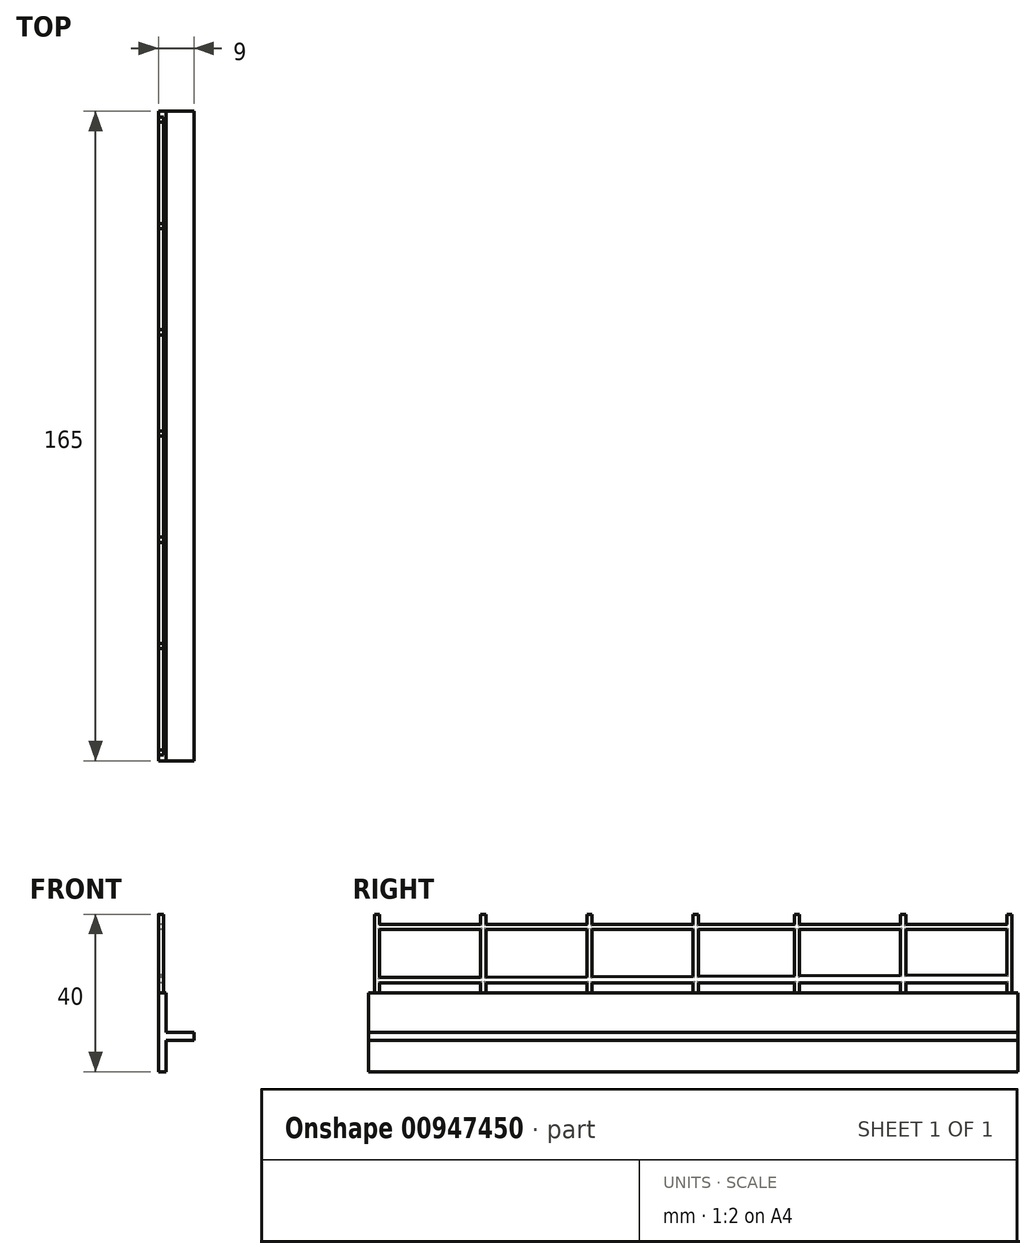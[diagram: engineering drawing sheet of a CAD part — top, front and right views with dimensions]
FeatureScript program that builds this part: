
annotation { "Feature Type Name" : "Feature", "Feature Type Description" : "" }
export const myFeature = defineFeature(function(context is Context, id is Id, definition is map)
    precondition{}
    {
        {
            var Q0;
            Q0=qCreatedBy(makeId("Front.planeOp"),FACE);
            var sketch = newSketch(context, id + "F0", { "sketchPlane" : qUnion([Q0])});
            skLineSegment(sketch, "E0", {"start": v(0, 0) * mm, "end": v(0, 10) * mm});
            skLineSegment(sketch, "E1", {"start": v(0, 0) * mm, "end": v(7, 0) * mm});
            skLineSegment(sketch, "E2", {"start": v(7, 0) * mm, "end": v(7, -2) * mm});
            skLineSegment(sketch, "E3", {"start": v(7, -2) * mm, "end": v(0, -2) * mm});
            skLineSegment(sketch, "E4", {"start": v(0, 10) * mm, "end": v(-2, 10) * mm});
            skLineSegment(sketch, "E5", {"start": v(0, -2) * mm, "end": v(0, -10) * mm});
            skLineSegment(sketch, "E6", {"start": v(-2, 10) * mm, "end": v(-2, -10) * mm});
            skLineSegment(sketch, "E7", {"start": v(0, -10) * mm, "end": v(-2, -10) * mm});
            skSolve(sketch);
        }
        {
            var Q0;
            Q0=makeQuery(id+"F0.imprint","IMPRINT",FACE,{"disambiguationData":[TD([[makeQuery(id+"F0.imprint","IMPRINT",EDGE,{"derivedFrom":sQuery(id+"F0.wireOp",EDGE,"E0")}),1.0]])]});
            extrude(context, id + "F1", {"entities" : qUnion([Q0]), "depth" : 165 * mm, "offsetDistance" : 25 * mm});
        }
        {
            var Q0;
            Q0=makeQuery(id+"F1.opExtrude","SWEPT_FACE",FACE,{"disambiguationData":[OSD([sQuery(id+"F0.wireOp",EDGE,"E4")])]});
            var sketch = newSketch(context, id + "F2", { "sketchPlane" : qUnion([Q0])});
            skLineSegment(sketch, "E8", {"start": v(0, 0) * mm, "end": v(0, -82.5) * mm});
            skLineSegment(sketch, "E9", {"start": v(0, -82.5) * mm, "end": v(0, -55.5) * mm});
            skLineSegment(sketch, "E10", {"start": v(0, -55.5) * mm, "end": v(0, -28.5) * mm});
            skLineSegment(sketch, "E11", {"start": v(0, -28.5) * mm, "end": v(0, -1.5) * mm});
            skLineSegment(sketch, "E12", {"start": v(0, -82.5) * mm, "end": v(0, -109.5) * mm});
            skLineSegment(sketch, "E13", {"start": v(0, -109.5) * mm, "end": v(0, -136.5) * mm});
            skLineSegment(sketch, "E14", {"start": v(0, -136.5) * mm, "end": v(0, -163.5) * mm});
            skLineSegment(sketch, "E15", {"start": v(-2, 0) * mm, "end": v(-0.7, 0) * mm});
            skLineSegment(sketch, "E16", {"start": v(-0.7, 0) * mm, "end": v(-0.7, -165) * mm});
            skLineSegment(sketch, "E17.bottom", {"start": v(-0.7, -1.5) * mm, "end": v(-2, -1.5) * mm});
            skLineSegment(sketch, "E17.top", {"start": v(-0.7, -2.8) * mm, "end": v(-2, -2.8) * mm});
            skLineSegment(sketch, "E17.left", {"start": v(-0.7, -1.5) * mm, "end": v(-0.7, -2.8) * mm});
            skLineSegment(sketch, "E17.right", {"start": v(-2, -1.5) * mm, "end": v(-2, -2.8) * mm});
            skLineSegment(sketch, "E18.bottom", {"start": v(-0.7, -28.5) * mm, "end": v(-2, -28.5) * mm});
            skLineSegment(sketch, "E18.top", {"start": v(-0.7, -29.8) * mm, "end": v(-2, -29.8) * mm});
            skLineSegment(sketch, "E18.left", {"start": v(-0.7, -28.5) * mm, "end": v(-0.7, -29.8) * mm});
            skLineSegment(sketch, "E18.right", {"start": v(-2, -28.5) * mm, "end": v(-2, -29.8) * mm});
            skLineSegment(sketch, "E19.bottom", {"start": v(-0.7, -55.5) * mm, "end": v(-2, -55.5) * mm});
            skLineSegment(sketch, "E19.top", {"start": v(-0.7, -56.8) * mm, "end": v(-2, -56.8) * mm});
            skLineSegment(sketch, "E19.left", {"start": v(-0.7, -55.5) * mm, "end": v(-0.7, -56.8) * mm});
            skLineSegment(sketch, "E19.right", {"start": v(-2, -55.5) * mm, "end": v(-2, -56.8) * mm});
            skLineSegment(sketch, "E20.bottom", {"start": v(-0.7, -82.5) * mm, "end": v(-2, -82.5) * mm});
            skLineSegment(sketch, "E20.top", {"start": v(-0.7, -81.2) * mm, "end": v(-2, -81.2) * mm});
            skLineSegment(sketch, "E20.left", {"start": v(-0.7, -82.5) * mm, "end": v(-0.7, -81.2) * mm});
            skLineSegment(sketch, "E20.right", {"start": v(-2, -82.5) * mm, "end": v(-2, -81.2) * mm});
            skLineSegment(sketch, "E21.bottom", {"start": v(-0.7, -109.5) * mm, "end": v(-2, -109.5) * mm});
            skLineSegment(sketch, "E21.top", {"start": v(-0.7, -108.2) * mm, "end": v(-2, -108.2) * mm});
            skLineSegment(sketch, "E21.left", {"start": v(-0.7, -109.5) * mm, "end": v(-0.7, -108.2) * mm});
            skLineSegment(sketch, "E21.right", {"start": v(-2, -109.5) * mm, "end": v(-2, -108.2) * mm});
            skLineSegment(sketch, "E22.bottom", {"start": v(-0.7, -136.5) * mm, "end": v(-2, -136.5) * mm});
            skLineSegment(sketch, "E22.top", {"start": v(-0.7, -135.2) * mm, "end": v(-2, -135.2) * mm});
            skLineSegment(sketch, "E22.left", {"start": v(-0.7, -136.5) * mm, "end": v(-0.7, -135.2) * mm});
            skLineSegment(sketch, "E22.right", {"start": v(-2, -136.5) * mm, "end": v(-2, -135.2) * mm});
            skLineSegment(sketch, "E23.bottom", {"start": v(-0.7, -163.5) * mm, "end": v(-2, -163.5) * mm});
            skLineSegment(sketch, "E23.top", {"start": v(-0.7, -162.2) * mm, "end": v(-2, -162.2) * mm});
            skLineSegment(sketch, "E23.left", {"start": v(-0.7, -163.5) * mm, "end": v(-0.7, -162.2) * mm});
            skLineSegment(sketch, "E23.right", {"start": v(-2, -163.5) * mm, "end": v(-2, -162.2) * mm});
            skSolve(sketch);
        }
        {
            var Q0;
            Q0=makeQuery(id+"F2.imprint","IMPRINT",FACE,{"disambiguationData":[TD([[makeQuery(id+"F2.imprint","IMPRINT",EDGE,{"derivedFrom":sQuery(id+"F2.wireOp",EDGE,"E17.bottom")}),1.0]])]});
            var Q1;
            Q1=makeQuery(id+"F2.imprint","IMPRINT",FACE,{"disambiguationData":[TD([[makeQuery(id+"F2.imprint","IMPRINT",EDGE,{"derivedFrom":sQuery(id+"F2.wireOp",EDGE,"E18.bottom")}),1.0]])]});
            var Q2;
            Q2=makeQuery(id+"F2.imprint","IMPRINT",FACE,{"disambiguationData":[TD([[makeQuery(id+"F2.imprint","IMPRINT",EDGE,{"derivedFrom":sQuery(id+"F2.wireOp",EDGE,"E19.bottom")}),1.0]])]});
            var Q3;
            Q3=makeQuery(id+"F2.imprint","IMPRINT",FACE,{"disambiguationData":[TD([[makeQuery(id+"F2.imprint","IMPRINT",EDGE,{"derivedFrom":sQuery(id+"F2.wireOp",EDGE,"E20.bottom")}),-1.0]])]});
            var Q4;
            Q4=makeQuery(id+"F2.imprint","IMPRINT",FACE,{"disambiguationData":[TD([[makeQuery(id+"F2.imprint","IMPRINT",EDGE,{"derivedFrom":sQuery(id+"F2.wireOp",EDGE,"E21.bottom")}),-1.0]])]});
            var Q5;
            Q5=makeQuery(id+"F2.imprint","IMPRINT",FACE,{"disambiguationData":[TD([[makeQuery(id+"F2.imprint","IMPRINT",EDGE,{"derivedFrom":sQuery(id+"F2.wireOp",EDGE,"E22.bottom")}),-1.0]])]});
            var Q6;
            Q6=makeQuery(id+"F2.imprint","IMPRINT",FACE,{"disambiguationData":[TD([[makeQuery(id+"F2.imprint","IMPRINT",EDGE,{"derivedFrom":sQuery(id+"F2.wireOp",EDGE,"E23.bottom")}),-1.0]])]});
            extrude(context, id + "F3", {"entities" : qUnion([Q0, Q1, Q2, Q3, Q4, Q5, Q6]), "operationType" : NewBodyOperationType.ADD, "depth" : 20 * mm, "offsetDistance" : 25 * mm});
        }
        {
            var Q0;
            Q0=makeQuery(id+"F3.boolean.opBoolean","MERGE",FACE,{"derivedFrom":[makeQuery(id+"F1.opExtrude","SWEPT_FACE",FACE,{"disambiguationData":[OSD([sQuery(id+"F0.wireOp",EDGE,"E6")])]}),makeQuery(id+"F3.opExtrude","SWEPT_FACE",FACE,{"disambiguationData":[OSD([sQuery(id+"F2.wireOp",EDGE,"E17.right")])]}),makeQuery(id+"F3.opExtrude","SWEPT_FACE",FACE,{"disambiguationData":[OSD([sQuery(id+"F2.wireOp",EDGE,"E18.right")])]}),makeQuery(id+"F3.opExtrude","SWEPT_FACE",FACE,{"disambiguationData":[OSD([sQuery(id+"F2.wireOp",EDGE,"E19.right")])]}),makeQuery(id+"F3.opExtrude","SWEPT_FACE",FACE,{"disambiguationData":[OSD([sQuery(id+"F2.wireOp",EDGE,"E20.right")])]}),makeQuery(id+"F3.opExtrude","SWEPT_FACE",FACE,{"disambiguationData":[OSD([sQuery(id+"F2.wireOp",EDGE,"E21.right")])]}),makeQuery(id+"F3.opExtrude","SWEPT_FACE",FACE,{"disambiguationData":[OSD([sQuery(id+"F2.wireOp",EDGE,"E22.right")])]}),makeQuery(id+"F3.opExtrude","SWEPT_FACE",FACE,{"disambiguationData":[OSD([sQuery(id+"F2.wireOp",EDGE,"E23.right")])]})]});
            var sketch = newSketch(context, id + "F4", { "sketchPlane" : qUnion([Q0])});
            skLineSegment(sketch, "E24", {"start": v(1.5, 10) * mm, "end": v(1.5, 12.6) * mm});
            skLineSegment(sketch, "E25", {"start": v(1.5, 12.6) * mm, "end": v(163.5, 12.6) * mm});
            skLineSegment(sketch, "E26", {"start": v(163.5, 12.6) * mm, "end": v(163.5, 13.9) * mm});
            skLineSegment(sketch, "E27", {"start": v(163.5, 13.9) * mm, "end": v(1.5, 14.56) * mm});
            skLineSegment(sketch, "E28", {"start": v(1.5, 30) * mm, "end": v(1.5, 27.4) * mm});
            skLineSegment(sketch, "E29", {"start": v(1.5, 27.4) * mm, "end": v(163.5, 27.4) * mm});
            skLineSegment(sketch, "E30", {"start": v(163.5, 27.4) * mm, "end": v(163.5, 26.1) * mm});
            skLineSegment(sketch, "E31", {"start": v(163.5, 26.1) * mm, "end": v(1.5, 26.1) * mm});
            skSolve(sketch);
        }
        {
            var Q0;
            {var subQ0=sQuery(id+"F4.wireOp",EDGE,"E25");var subQ1=sQuery(id+"F0.wireOp",EDGE,"E6");var subQ2=sQuery(id+"F0.wireOp",EDGE,"E4");var subQ3=makeQuery(id+"F3.opExtrude","SWEPT_EDGE",EDGE,{"disambiguationData":[OSD([subQ2,subQ1,sQuery(id+"F2.wireOp",EDGE,"E17.top"),sQuery(id+"F2.wireOp",EDGE,"E17.right")])]});var subQ4=makeQuery(id+"F4.imprint","INTERSECT",VERTEX,{"derivedFrom":[subQ3,subQ0]});Q0=makeQuery(id+"F4.imprint","IMPRINT",FACE,{"disambiguationData":[TD([[makeQuery(id+"F4.imprint","IMPRINT",EDGE,{"disambiguationData":[TD([[subQ4,-1.0]])],"derivedFrom":subQ0}),1.0]])]});}
            var Q1;
            {var subQ0=sQuery(id+"F4.wireOp",EDGE,"E29");var subQ1=sQuery(id+"F0.wireOp",EDGE,"E6");var subQ2=sQuery(id+"F0.wireOp",EDGE,"E4");var subQ3=makeQuery(id+"F3.opExtrude","SWEPT_EDGE",EDGE,{"disambiguationData":[OSD([subQ2,subQ1,sQuery(id+"F2.wireOp",EDGE,"E17.top"),sQuery(id+"F2.wireOp",EDGE,"E17.right")])]});var subQ4=makeQuery(id+"F4.imprint","INTERSECT",VERTEX,{"derivedFrom":[subQ3,subQ0]});Q1=makeQuery(id+"F4.imprint","IMPRINT",FACE,{"disambiguationData":[TD([[makeQuery(id+"F4.imprint","IMPRINT",EDGE,{"disambiguationData":[TD([[subQ4,-1.0]])],"derivedFrom":subQ0}),-1.0]])]});}
            var Q2;
            {var subQ0=sQuery(id+"F4.wireOp",EDGE,"E29");var subQ1=sQuery(id+"F0.wireOp",EDGE,"E6");var subQ2=sQuery(id+"F0.wireOp",EDGE,"E4");var subQ3=makeQuery(id+"F3.opExtrude","SWEPT_EDGE",EDGE,{"disambiguationData":[OSD([subQ2,subQ1,sQuery(id+"F2.wireOp",EDGE,"E18.top"),sQuery(id+"F2.wireOp",EDGE,"E18.right")])]});var subQ4=makeQuery(id+"F4.imprint","INTERSECT",VERTEX,{"derivedFrom":[subQ3,subQ0]});Q2=makeQuery(id+"F4.imprint","IMPRINT",FACE,{"disambiguationData":[TD([[makeQuery(id+"F4.imprint","IMPRINT",EDGE,{"disambiguationData":[TD([[subQ4,-1.0]])],"derivedFrom":subQ0}),-1.0]])]});}
            var Q3;
            {var subQ0=sQuery(id+"F4.wireOp",EDGE,"E25");var subQ1=sQuery(id+"F0.wireOp",EDGE,"E6");var subQ2=sQuery(id+"F0.wireOp",EDGE,"E4");var subQ3=makeQuery(id+"F3.opExtrude","SWEPT_EDGE",EDGE,{"disambiguationData":[OSD([subQ2,subQ1,sQuery(id+"F2.wireOp",EDGE,"E18.top"),sQuery(id+"F2.wireOp",EDGE,"E18.right")])]});var subQ4=makeQuery(id+"F4.imprint","INTERSECT",VERTEX,{"derivedFrom":[subQ3,subQ0]});Q3=makeQuery(id+"F4.imprint","IMPRINT",FACE,{"disambiguationData":[TD([[makeQuery(id+"F4.imprint","IMPRINT",EDGE,{"disambiguationData":[TD([[subQ4,-1.0]])],"derivedFrom":subQ0}),1.0]])]});}
            var Q4;
            {var subQ0=sQuery(id+"F4.wireOp",EDGE,"E29");var subQ1=sQuery(id+"F0.wireOp",EDGE,"E6");var subQ2=sQuery(id+"F0.wireOp",EDGE,"E4");var subQ3=makeQuery(id+"F3.opExtrude","SWEPT_EDGE",EDGE,{"disambiguationData":[OSD([subQ2,subQ1,sQuery(id+"F2.wireOp",EDGE,"E19.top"),sQuery(id+"F2.wireOp",EDGE,"E19.right")])]});var subQ4=makeQuery(id+"F4.imprint","INTERSECT",VERTEX,{"derivedFrom":[subQ3,subQ0]});Q4=makeQuery(id+"F4.imprint","IMPRINT",FACE,{"disambiguationData":[TD([[makeQuery(id+"F4.imprint","IMPRINT",EDGE,{"disambiguationData":[TD([[subQ4,-1.0]])],"derivedFrom":subQ0}),-1.0]])]});}
            var Q5;
            {var subQ0=sQuery(id+"F4.wireOp",EDGE,"E25");var subQ1=sQuery(id+"F0.wireOp",EDGE,"E6");var subQ2=sQuery(id+"F0.wireOp",EDGE,"E4");var subQ3=makeQuery(id+"F3.opExtrude","SWEPT_EDGE",EDGE,{"disambiguationData":[OSD([subQ2,subQ1,sQuery(id+"F2.wireOp",EDGE,"E19.top"),sQuery(id+"F2.wireOp",EDGE,"E19.right")])]});var subQ4=makeQuery(id+"F4.imprint","INTERSECT",VERTEX,{"derivedFrom":[subQ3,subQ0]});Q5=makeQuery(id+"F4.imprint","IMPRINT",FACE,{"disambiguationData":[TD([[makeQuery(id+"F4.imprint","IMPRINT",EDGE,{"disambiguationData":[TD([[subQ4,-1.0]])],"derivedFrom":subQ0}),1.0]])]});}
            var Q6;
            {var subQ0=sQuery(id+"F4.wireOp",EDGE,"E25");var subQ1=sQuery(id+"F0.wireOp",EDGE,"E6");var subQ2=sQuery(id+"F0.wireOp",EDGE,"E4");var subQ3=makeQuery(id+"F3.opExtrude","SWEPT_EDGE",EDGE,{"disambiguationData":[OSD([subQ2,subQ1,sQuery(id+"F2.wireOp",EDGE,"E20.bottom"),sQuery(id+"F2.wireOp",EDGE,"E20.right")])]});var subQ4=makeQuery(id+"F4.imprint","INTERSECT",VERTEX,{"derivedFrom":[subQ3,subQ0]});Q6=makeQuery(id+"F4.imprint","IMPRINT",FACE,{"disambiguationData":[TD([[makeQuery(id+"F4.imprint","IMPRINT",EDGE,{"disambiguationData":[TD([[subQ4,-1.0]])],"derivedFrom":subQ0}),1.0]])]});}
            var Q7;
            {var subQ0=sQuery(id+"F4.wireOp",EDGE,"E29");var subQ1=sQuery(id+"F0.wireOp",EDGE,"E6");var subQ2=sQuery(id+"F0.wireOp",EDGE,"E4");var subQ3=makeQuery(id+"F3.opExtrude","SWEPT_EDGE",EDGE,{"disambiguationData":[OSD([subQ2,subQ1,sQuery(id+"F2.wireOp",EDGE,"E20.bottom"),sQuery(id+"F2.wireOp",EDGE,"E20.right")])]});var subQ4=makeQuery(id+"F4.imprint","INTERSECT",VERTEX,{"derivedFrom":[subQ3,subQ0]});Q7=makeQuery(id+"F4.imprint","IMPRINT",FACE,{"disambiguationData":[TD([[makeQuery(id+"F4.imprint","IMPRINT",EDGE,{"disambiguationData":[TD([[subQ4,-1.0]])],"derivedFrom":subQ0}),-1.0]])]});}
            var Q8;
            {var subQ0=sQuery(id+"F4.wireOp",EDGE,"E29");var subQ1=sQuery(id+"F0.wireOp",EDGE,"E6");var subQ2=sQuery(id+"F0.wireOp",EDGE,"E4");var subQ3=makeQuery(id+"F3.opExtrude","SWEPT_EDGE",EDGE,{"disambiguationData":[OSD([subQ2,subQ1,sQuery(id+"F2.wireOp",EDGE,"E21.bottom"),sQuery(id+"F2.wireOp",EDGE,"E21.right")])]});var subQ4=makeQuery(id+"F4.imprint","INTERSECT",VERTEX,{"derivedFrom":[subQ3,subQ0]});Q8=makeQuery(id+"F4.imprint","IMPRINT",FACE,{"disambiguationData":[TD([[makeQuery(id+"F4.imprint","IMPRINT",EDGE,{"disambiguationData":[TD([[subQ4,-1.0]])],"derivedFrom":subQ0}),-1.0]])]});}
            var Q9;
            {var subQ0=sQuery(id+"F4.wireOp",EDGE,"E25");var subQ1=sQuery(id+"F0.wireOp",EDGE,"E6");var subQ2=sQuery(id+"F0.wireOp",EDGE,"E4");var subQ3=makeQuery(id+"F3.opExtrude","SWEPT_EDGE",EDGE,{"disambiguationData":[OSD([subQ2,subQ1,sQuery(id+"F2.wireOp",EDGE,"E21.bottom"),sQuery(id+"F2.wireOp",EDGE,"E21.right")])]});var subQ4=makeQuery(id+"F4.imprint","INTERSECT",VERTEX,{"derivedFrom":[subQ3,subQ0]});Q9=makeQuery(id+"F4.imprint","IMPRINT",FACE,{"disambiguationData":[TD([[makeQuery(id+"F4.imprint","IMPRINT",EDGE,{"disambiguationData":[TD([[subQ4,-1.0]])],"derivedFrom":subQ0}),1.0]])]});}
            var Q10;
            {var subQ0=sQuery(id+"F4.wireOp",EDGE,"E25");var subQ1=sQuery(id+"F0.wireOp",EDGE,"E6");var subQ2=sQuery(id+"F0.wireOp",EDGE,"E4");var subQ3=makeQuery(id+"F3.opExtrude","SWEPT_EDGE",EDGE,{"disambiguationData":[OSD([subQ2,subQ1,sQuery(id+"F2.wireOp",EDGE,"E22.bottom"),sQuery(id+"F2.wireOp",EDGE,"E22.right")])]});var subQ4=makeQuery(id+"F4.imprint","INTERSECT",VERTEX,{"derivedFrom":[subQ3,subQ0]});Q10=makeQuery(id+"F4.imprint","IMPRINT",FACE,{"disambiguationData":[TD([[makeQuery(id+"F4.imprint","IMPRINT",EDGE,{"disambiguationData":[TD([[subQ4,-1.0]])],"derivedFrom":subQ0}),1.0]])]});}
            var Q11;
            {var subQ0=sQuery(id+"F4.wireOp",EDGE,"E29");var subQ1=sQuery(id+"F0.wireOp",EDGE,"E6");var subQ2=sQuery(id+"F0.wireOp",EDGE,"E4");var subQ3=makeQuery(id+"F3.opExtrude","SWEPT_EDGE",EDGE,{"disambiguationData":[OSD([subQ2,subQ1,sQuery(id+"F2.wireOp",EDGE,"E22.bottom"),sQuery(id+"F2.wireOp",EDGE,"E22.right")])]});var subQ4=makeQuery(id+"F4.imprint","INTERSECT",VERTEX,{"derivedFrom":[subQ3,subQ0]});Q11=makeQuery(id+"F4.imprint","IMPRINT",FACE,{"disambiguationData":[TD([[makeQuery(id+"F4.imprint","IMPRINT",EDGE,{"disambiguationData":[TD([[subQ4,-1.0]])],"derivedFrom":subQ0}),-1.0]])]});}
            extrude(context, id + "F5", {"entities" : qUnion([Q0, Q1, Q2, Q3, Q4, Q5, Q6, Q7, Q8, Q9, Q10, Q11]), "operationType" : NewBodyOperationType.ADD, "oppositeDirection" : true, "depth" : 1.3 * mm, "offsetDistance" : 25 * mm});
        }
        {
            var Q0;
            {var subQ6=sQuery(id+"F0.wireOp",EDGE,"E6");var subQ7=sQuery(id+"F0.wireOp",EDGE,"E4");var subQ17=sQuery(id+"F2.wireOp",EDGE,"E22.right");var subQ18=sQuery(id+"F2.wireOp",EDGE,"E22.top");var subQ20=makeQuery(id+"F3.opExtrude","SWEPT_EDGE",EDGE,{"disambiguationData":[OSD([subQ7,subQ6,subQ18,subQ17])]});Q0=makeQuery(id+"F5.boolean.opBoolean","SPLIT",EDGE,{"disambiguationData":[TD([makeQuery(id+"F1.opExtrude","SWEPT_FACE",FACE,{"disambiguationData":[OSD([subQ7])]})])],"derivedFrom":subQ20});}
            var Q1;
            {var subQ6=sQuery(id+"F0.wireOp",EDGE,"E6");var subQ7=sQuery(id+"F0.wireOp",EDGE,"E4");var subQ17=sQuery(id+"F2.wireOp",EDGE,"E22.right");var subQ20=sQuery(id+"F2.wireOp",EDGE,"E22.bottom");var subQ21=makeQuery(id+"F3.opExtrude","SWEPT_EDGE",EDGE,{"disambiguationData":[OSD([subQ7,subQ6,subQ20,subQ17])]});Q1=makeQuery(id+"F5.boolean.opBoolean","SPLIT",EDGE,{"disambiguationData":[TD([makeQuery(id+"F1.opExtrude","SWEPT_FACE",FACE,{"disambiguationData":[OSD([subQ7])]})])],"derivedFrom":subQ21});}
            var Q2;
            {var subQ0=sQuery(id+"F4.wireOp",EDGE,"E25");var subQ1=sQuery(id+"F0.wireOp",EDGE,"E6");var subQ2=sQuery(id+"F0.wireOp",EDGE,"E4");Q2=makeQuery(id+"F5.opExtrude","CAP_EDGE",EDGE,{"disambiguationData":[OSD([subQ0]),TDD([makeQuery(id+"F4.imprint","IMPRINT",EDGE,{"disambiguationData":[TD([[makeQuery(id+"F4.imprint","INTERSECT",VERTEX,{"derivedFrom":[makeQuery(id+"F3.opExtrude","SWEPT_EDGE",EDGE,{"disambiguationData":[OSD([subQ2,subQ1,sQuery(id+"F2.wireOp",EDGE,"E22.bottom"),sQuery(id+"F2.wireOp",EDGE,"E22.right")])]}),subQ0]}),-1.0]])],"derivedFrom":subQ0})])],"isStart":true});}
            var Q3;
            {var subQ0=sQuery(id+"F4.wireOp",EDGE,"E27");var subQ1=sQuery(id+"F0.wireOp",EDGE,"E6");var subQ2=sQuery(id+"F0.wireOp",EDGE,"E4");Q3=makeQuery(id+"F5.opExtrude","CAP_EDGE",EDGE,{"disambiguationData":[OSD([subQ0]),TDD([makeQuery(id+"F4.imprint","IMPRINT",EDGE,{"disambiguationData":[TD([[makeQuery(id+"F4.imprint","INTERSECT",VERTEX,{"derivedFrom":[makeQuery(id+"F3.opExtrude","SWEPT_EDGE",EDGE,{"disambiguationData":[OSD([subQ2,subQ1,sQuery(id+"F2.wireOp",EDGE,"E23.top"),sQuery(id+"F2.wireOp",EDGE,"E23.right")])]}),subQ0]}),-1.0]])],"derivedFrom":subQ0})])],"isStart":true});}
            var Q4;
            {var subQ6=sQuery(id+"F0.wireOp",EDGE,"E6");var subQ7=sQuery(id+"F0.wireOp",EDGE,"E4");var subQ21=sQuery(id+"F2.wireOp",EDGE,"E23.right");var subQ22=sQuery(id+"F2.wireOp",EDGE,"E23.top");var subQ23=makeQuery(id+"F3.opExtrude","SWEPT_EDGE",EDGE,{"disambiguationData":[OSD([subQ7,subQ6,subQ22,subQ21])]});Q4=makeQuery(id+"F5.boolean.opBoolean","SPLIT",EDGE,{"disambiguationData":[TD([makeQuery(id+"F1.opExtrude","SWEPT_FACE",FACE,{"disambiguationData":[OSD([subQ7])]})])],"derivedFrom":subQ23});}
            var Q5;
            Q5=makeQuery(id+"F3.opExtrude","SWEPT_EDGE",EDGE,{"disambiguationData":[OSD([sQuery(id+"F0.wireOp",EDGE,"E4"),sQuery(id+"F0.wireOp",EDGE,"E6"),sQuery(id+"F2.wireOp",EDGE,"E23.bottom"),sQuery(id+"F2.wireOp",EDGE,"E23.right")])]});
            var Q6;
            {var subQ2=sQuery(id+"F2.wireOp",EDGE,"E23.right");var subQ3=sQuery(id+"F2.wireOp",EDGE,"E23.top");var subQ6=sQuery(id+"F0.wireOp",EDGE,"E6");var subQ7=sQuery(id+"F0.wireOp",EDGE,"E4");var subQ19=sQuery(id+"F4.wireOp",EDGE,"E27");var subQ20=makeQuery(id+"F3.opExtrude","SWEPT_EDGE",EDGE,{"disambiguationData":[OSD([subQ7,subQ6,subQ3,subQ2])]});Q6=makeQuery(id+"F5.boolean.opBoolean","SPLIT",EDGE,{"disambiguationData":[TD([makeQuery(id+"F5.opExtrude","SWEPT_FACE",FACE,{"disambiguationData":[OSD([subQ19]),TDD([makeQuery(id+"F4.imprint","IMPRINT",EDGE,{"disambiguationData":[TD([[makeQuery(id+"F4.imprint","INTERSECT",VERTEX,{"derivedFrom":[subQ20,subQ19]}),-1.0]])],"derivedFrom":subQ19})])]})])],"derivedFrom":subQ20});}
            var Q7;
            {var subQ0=sQuery(id+"F4.wireOp",EDGE,"E29");var subQ1=sQuery(id+"F0.wireOp",EDGE,"E6");var subQ2=sQuery(id+"F0.wireOp",EDGE,"E4");Q7=makeQuery(id+"F5.opExtrude","CAP_EDGE",EDGE,{"disambiguationData":[OSD([subQ0]),TDD([makeQuery(id+"F4.imprint","IMPRINT",EDGE,{"disambiguationData":[TD([[makeQuery(id+"F4.imprint","INTERSECT",VERTEX,{"derivedFrom":[makeQuery(id+"F3.opExtrude","SWEPT_EDGE",EDGE,{"disambiguationData":[OSD([subQ2,subQ1,sQuery(id+"F2.wireOp",EDGE,"E22.bottom"),sQuery(id+"F2.wireOp",EDGE,"E22.right")])]}),subQ0]}),-1.0]])],"derivedFrom":subQ0})])],"isStart":true});}
            var Q8;
            {var subQ0=sQuery(id+"F4.wireOp",EDGE,"E31");var subQ1=sQuery(id+"F0.wireOp",EDGE,"E6");var subQ2=sQuery(id+"F0.wireOp",EDGE,"E4");Q8=makeQuery(id+"F5.opExtrude","CAP_EDGE",EDGE,{"disambiguationData":[OSD([subQ0]),TDD([makeQuery(id+"F4.imprint","IMPRINT",EDGE,{"disambiguationData":[TD([[makeQuery(id+"F4.imprint","INTERSECT",VERTEX,{"derivedFrom":[makeQuery(id+"F3.opExtrude","SWEPT_EDGE",EDGE,{"disambiguationData":[OSD([subQ2,subQ1,sQuery(id+"F2.wireOp",EDGE,"E23.top"),sQuery(id+"F2.wireOp",EDGE,"E23.right")])]}),subQ0]}),-1.0]])],"derivedFrom":subQ0})])],"isStart":true});}
            var Q9;
            {var subQ6=sQuery(id+"F0.wireOp",EDGE,"E6");var subQ7=sQuery(id+"F0.wireOp",EDGE,"E4");var subQ15=sQuery(id+"F4.wireOp",EDGE,"E27");var subQ16=sQuery(id+"F2.wireOp",EDGE,"E23.right");var subQ17=sQuery(id+"F2.wireOp",EDGE,"E23.top");var subQ18=makeQuery(id+"F3.opExtrude","SWEPT_EDGE",EDGE,{"disambiguationData":[OSD([subQ7,subQ6,subQ17,subQ16])]});var subQ19=sQuery(id+"F2.wireOp",EDGE,"E22.right");var subQ20=sQuery(id+"F2.wireOp",EDGE,"E22.bottom");var subQ21=makeQuery(id+"F3.opExtrude","SWEPT_EDGE",EDGE,{"disambiguationData":[OSD([subQ7,subQ6,subQ20,subQ19])]});Q9=makeQuery(id+"F5.boolean.opBoolean","SPLIT",EDGE,{"disambiguationData":[TD([makeQuery(id+"F5.opExtrude","SWEPT_FACE",FACE,{"disambiguationData":[OSD([subQ15]),TDD([makeQuery(id+"F4.imprint","IMPRINT",EDGE,{"disambiguationData":[TD([[makeQuery(id+"F4.imprint","INTERSECT",VERTEX,{"derivedFrom":[subQ18,subQ15]}),-1.0]])],"derivedFrom":subQ15})])]})])],"derivedFrom":subQ21});}
            var Q10;
            {var subQ6=sQuery(id+"F0.wireOp",EDGE,"E6");var subQ7=sQuery(id+"F0.wireOp",EDGE,"E4");var subQ17=sQuery(id+"F2.wireOp",EDGE,"E22.right");var subQ18=sQuery(id+"F2.wireOp",EDGE,"E22.top");var subQ22=sQuery(id+"F2.wireOp",EDGE,"E22.bottom");var subQ23=makeQuery(id+"F3.opExtrude","SWEPT_EDGE",EDGE,{"disambiguationData":[OSD([subQ7,subQ6,subQ22,subQ17])]});Q10=makeQuery(id+"F5.boolean.opBoolean","SPLIT",EDGE,{"disambiguationData":[TD([makeQuery(id+"F3.opExtrude","CAP_FACE",FACE,{"disambiguationData":[OSD([subQ22,subQ18,sQuery(id+"F2.wireOp",EDGE,"E22.left"),subQ17])],"isStart":false})])],"derivedFrom":subQ23});}
            var Q11;
            {var subQ6=sQuery(id+"F0.wireOp",EDGE,"E6");var subQ7=sQuery(id+"F0.wireOp",EDGE,"E4");var subQ16=sQuery(id+"F2.wireOp",EDGE,"E22.right");var subQ17=sQuery(id+"F2.wireOp",EDGE,"E22.top");var subQ18=makeQuery(id+"F3.opExtrude","SWEPT_EDGE",EDGE,{"disambiguationData":[OSD([subQ7,subQ6,subQ17,subQ16])]});var subQ25=sQuery(id+"F2.wireOp",EDGE,"E22.bottom");Q11=makeQuery(id+"F5.boolean.opBoolean","SPLIT",EDGE,{"disambiguationData":[TD([makeQuery(id+"F3.opExtrude","CAP_FACE",FACE,{"disambiguationData":[OSD([subQ25,subQ17,sQuery(id+"F2.wireOp",EDGE,"E22.left"),subQ16])],"isStart":false})])],"derivedFrom":subQ18});}
            var Q12;
            {var subQ4=sQuery(id+"F2.wireOp",EDGE,"E22.right");var subQ6=sQuery(id+"F0.wireOp",EDGE,"E6");var subQ7=sQuery(id+"F0.wireOp",EDGE,"E4");var subQ19=sQuery(id+"F4.wireOp",EDGE,"E27");var subQ20=sQuery(id+"F2.wireOp",EDGE,"E22.top");var subQ21=makeQuery(id+"F3.opExtrude","SWEPT_EDGE",EDGE,{"disambiguationData":[OSD([subQ7,subQ6,subQ20,subQ4])]});Q12=makeQuery(id+"F5.boolean.opBoolean","SPLIT",EDGE,{"disambiguationData":[TD([makeQuery(id+"F5.opExtrude","SWEPT_FACE",FACE,{"disambiguationData":[OSD([subQ19]),TDD([makeQuery(id+"F4.imprint","IMPRINT",EDGE,{"disambiguationData":[TD([[makeQuery(id+"F4.imprint","INTERSECT",VERTEX,{"derivedFrom":[subQ21,subQ19]}),-1.0]])],"derivedFrom":subQ19})])]})])],"derivedFrom":subQ21});}
            var Q13;
            {var subQ0=sQuery(id+"F4.wireOp",EDGE,"E27");var subQ1=sQuery(id+"F0.wireOp",EDGE,"E6");var subQ2=sQuery(id+"F0.wireOp",EDGE,"E4");Q13=makeQuery(id+"F5.opExtrude","CAP_EDGE",EDGE,{"disambiguationData":[OSD([subQ0]),TDD([makeQuery(id+"F4.imprint","IMPRINT",EDGE,{"disambiguationData":[TD([[makeQuery(id+"F4.imprint","INTERSECT",VERTEX,{"derivedFrom":[makeQuery(id+"F3.opExtrude","SWEPT_EDGE",EDGE,{"disambiguationData":[OSD([subQ2,subQ1,sQuery(id+"F2.wireOp",EDGE,"E22.top"),sQuery(id+"F2.wireOp",EDGE,"E22.right")])]}),subQ0]}),-1.0]])],"derivedFrom":subQ0})])],"isStart":true});}
            var Q14;
            {var subQ0=sQuery(id+"F4.wireOp",EDGE,"E25");var subQ1=sQuery(id+"F0.wireOp",EDGE,"E6");var subQ2=sQuery(id+"F0.wireOp",EDGE,"E4");Q14=makeQuery(id+"F5.opExtrude","CAP_EDGE",EDGE,{"disambiguationData":[OSD([subQ0]),TDD([makeQuery(id+"F4.imprint","IMPRINT",EDGE,{"disambiguationData":[TD([[makeQuery(id+"F4.imprint","INTERSECT",VERTEX,{"derivedFrom":[makeQuery(id+"F3.opExtrude","SWEPT_EDGE",EDGE,{"disambiguationData":[OSD([subQ2,subQ1,sQuery(id+"F2.wireOp",EDGE,"E21.bottom"),sQuery(id+"F2.wireOp",EDGE,"E21.right")])]}),subQ0]}),-1.0]])],"derivedFrom":subQ0})])],"isStart":true});}
            var Q15;
            {var subQ0=sQuery(id+"F4.wireOp",EDGE,"E31");var subQ1=sQuery(id+"F0.wireOp",EDGE,"E6");var subQ2=sQuery(id+"F0.wireOp",EDGE,"E4");Q15=makeQuery(id+"F5.opExtrude","CAP_EDGE",EDGE,{"disambiguationData":[OSD([subQ0]),TDD([makeQuery(id+"F4.imprint","IMPRINT",EDGE,{"disambiguationData":[TD([[makeQuery(id+"F4.imprint","INTERSECT",VERTEX,{"derivedFrom":[makeQuery(id+"F3.opExtrude","SWEPT_EDGE",EDGE,{"disambiguationData":[OSD([subQ2,subQ1,sQuery(id+"F2.wireOp",EDGE,"E22.top"),sQuery(id+"F2.wireOp",EDGE,"E22.right")])]}),subQ0]}),-1.0]])],"derivedFrom":subQ0})])],"isStart":true});}
            var Q16;
            {var subQ0=sQuery(id+"F4.wireOp",EDGE,"E29");var subQ1=sQuery(id+"F0.wireOp",EDGE,"E6");var subQ2=sQuery(id+"F0.wireOp",EDGE,"E4");Q16=makeQuery(id+"F5.opExtrude","CAP_EDGE",EDGE,{"disambiguationData":[OSD([subQ0]),TDD([makeQuery(id+"F4.imprint","IMPRINT",EDGE,{"disambiguationData":[TD([[makeQuery(id+"F4.imprint","INTERSECT",VERTEX,{"derivedFrom":[makeQuery(id+"F3.opExtrude","SWEPT_EDGE",EDGE,{"disambiguationData":[OSD([subQ2,subQ1,sQuery(id+"F2.wireOp",EDGE,"E21.bottom"),sQuery(id+"F2.wireOp",EDGE,"E21.right")])]}),subQ0]}),-1.0]])],"derivedFrom":subQ0})])],"isStart":true});}
            var Q17;
            {var subQ6=sQuery(id+"F0.wireOp",EDGE,"E6");var subQ7=sQuery(id+"F0.wireOp",EDGE,"E4");var subQ22=sQuery(id+"F2.wireOp",EDGE,"E23.top");var subQ23=sQuery(id+"F2.wireOp",EDGE,"E23.right");var subQ25=makeQuery(id+"F3.opExtrude","SWEPT_EDGE",EDGE,{"disambiguationData":[OSD([subQ7,subQ6,subQ22,subQ23])]});Q17=makeQuery(id+"F5.boolean.opBoolean","SPLIT",EDGE,{"disambiguationData":[TD([makeQuery(id+"F3.opExtrude","CAP_FACE",FACE,{"disambiguationData":[OSD([sQuery(id+"F2.wireOp",EDGE,"E23.bottom"),subQ22,sQuery(id+"F2.wireOp",EDGE,"E23.left"),subQ23])],"isStart":false})])],"derivedFrom":subQ25});}
            var Q18;
            {var subQ6=sQuery(id+"F0.wireOp",EDGE,"E6");var subQ7=sQuery(id+"F0.wireOp",EDGE,"E4");var subQ18=sQuery(id+"F2.wireOp",EDGE,"E21.right");var subQ19=sQuery(id+"F2.wireOp",EDGE,"E21.bottom");var subQ23=sQuery(id+"F2.wireOp",EDGE,"E21.top");var subQ25=makeQuery(id+"F3.opExtrude","SWEPT_EDGE",EDGE,{"disambiguationData":[OSD([subQ7,subQ6,subQ19,subQ18])]});Q18=makeQuery(id+"F5.boolean.opBoolean","SPLIT",EDGE,{"disambiguationData":[TD([makeQuery(id+"F3.opExtrude","CAP_FACE",FACE,{"disambiguationData":[OSD([subQ19,subQ23,sQuery(id+"F2.wireOp",EDGE,"E21.left"),subQ18])],"isStart":false})])],"derivedFrom":subQ25});}
            var Q19;
            {var subQ0=sQuery(id+"F4.wireOp",EDGE,"E29");var subQ1=sQuery(id+"F0.wireOp",EDGE,"E6");var subQ2=sQuery(id+"F0.wireOp",EDGE,"E4");Q19=makeQuery(id+"F5.opExtrude","CAP_EDGE",EDGE,{"disambiguationData":[OSD([subQ0]),TDD([makeQuery(id+"F4.imprint","IMPRINT",EDGE,{"disambiguationData":[TD([[makeQuery(id+"F4.imprint","INTERSECT",VERTEX,{"derivedFrom":[makeQuery(id+"F3.opExtrude","SWEPT_EDGE",EDGE,{"disambiguationData":[OSD([subQ2,subQ1,sQuery(id+"F2.wireOp",EDGE,"E20.bottom"),sQuery(id+"F2.wireOp",EDGE,"E20.right")])]}),subQ0]}),-1.0]])],"derivedFrom":subQ0})])],"isStart":true});}
            var Q20;
            {var subQ0=sQuery(id+"F4.wireOp",EDGE,"E27");var subQ1=sQuery(id+"F0.wireOp",EDGE,"E6");var subQ2=sQuery(id+"F0.wireOp",EDGE,"E4");Q20=makeQuery(id+"F5.opExtrude","CAP_EDGE",EDGE,{"disambiguationData":[OSD([subQ0]),TDD([makeQuery(id+"F4.imprint","IMPRINT",EDGE,{"disambiguationData":[TD([[makeQuery(id+"F4.imprint","INTERSECT",VERTEX,{"derivedFrom":[makeQuery(id+"F3.opExtrude","SWEPT_EDGE",EDGE,{"disambiguationData":[OSD([subQ2,subQ1,sQuery(id+"F2.wireOp",EDGE,"E21.top"),sQuery(id+"F2.wireOp",EDGE,"E21.right")])]}),subQ0]}),-1.0]])],"derivedFrom":subQ0})])],"isStart":true});}
            var Q21;
            {var subQ6=sQuery(id+"F0.wireOp",EDGE,"E6");var subQ7=sQuery(id+"F0.wireOp",EDGE,"E4");var subQ8=sQuery(id+"F2.wireOp",EDGE,"E21.right");var subQ9=sQuery(id+"F2.wireOp",EDGE,"E21.top");var subQ19=sQuery(id+"F4.wireOp",EDGE,"E27");var subQ20=makeQuery(id+"F3.opExtrude","SWEPT_EDGE",EDGE,{"disambiguationData":[OSD([subQ7,subQ6,subQ9,subQ8])]});Q21=makeQuery(id+"F5.boolean.opBoolean","SPLIT",EDGE,{"disambiguationData":[TD([makeQuery(id+"F5.opExtrude","SWEPT_FACE",FACE,{"disambiguationData":[OSD([subQ19]),TDD([makeQuery(id+"F4.imprint","IMPRINT",EDGE,{"disambiguationData":[TD([[makeQuery(id+"F4.imprint","INTERSECT",VERTEX,{"derivedFrom":[subQ20,subQ19]}),-1.0]])],"derivedFrom":subQ19})])]})])],"derivedFrom":subQ20});}
            var Q22;
            {var subQ0=sQuery(id+"F4.wireOp",EDGE,"E25");var subQ1=sQuery(id+"F0.wireOp",EDGE,"E6");var subQ2=sQuery(id+"F0.wireOp",EDGE,"E4");Q22=makeQuery(id+"F5.opExtrude","CAP_EDGE",EDGE,{"disambiguationData":[OSD([subQ0]),TDD([makeQuery(id+"F4.imprint","IMPRINT",EDGE,{"disambiguationData":[TD([[makeQuery(id+"F4.imprint","INTERSECT",VERTEX,{"derivedFrom":[makeQuery(id+"F3.opExtrude","SWEPT_EDGE",EDGE,{"disambiguationData":[OSD([subQ2,subQ1,sQuery(id+"F2.wireOp",EDGE,"E20.bottom"),sQuery(id+"F2.wireOp",EDGE,"E20.right")])]}),subQ0]}),-1.0]])],"derivedFrom":subQ0})])],"isStart":true});}
            var Q23;
            {var subQ2=sQuery(id+"F2.wireOp",EDGE,"E21.right");var subQ3=sQuery(id+"F2.wireOp",EDGE,"E21.top");var subQ6=sQuery(id+"F0.wireOp",EDGE,"E6");var subQ7=sQuery(id+"F0.wireOp",EDGE,"E4");var subQ20=makeQuery(id+"F3.opExtrude","SWEPT_EDGE",EDGE,{"disambiguationData":[OSD([subQ7,subQ6,subQ3,subQ2])]});Q23=makeQuery(id+"F5.boolean.opBoolean","SPLIT",EDGE,{"disambiguationData":[TD([makeQuery(id+"F1.opExtrude","SWEPT_FACE",FACE,{"disambiguationData":[OSD([subQ7])]})])],"derivedFrom":subQ20});}
            var Q24;
            {var subQ6=sQuery(id+"F0.wireOp",EDGE,"E6");var subQ7=sQuery(id+"F0.wireOp",EDGE,"E4");var subQ8=sQuery(id+"F2.wireOp",EDGE,"E21.right");var subQ9=sQuery(id+"F2.wireOp",EDGE,"E21.top");var subQ10=sQuery(id+"F2.wireOp",EDGE,"E20.right");var subQ11=sQuery(id+"F2.wireOp",EDGE,"E20.bottom");var subQ19=sQuery(id+"F4.wireOp",EDGE,"E27");var subQ20=makeQuery(id+"F3.opExtrude","SWEPT_EDGE",EDGE,{"disambiguationData":[OSD([subQ7,subQ6,subQ9,subQ8])]});var subQ21=makeQuery(id+"F3.opExtrude","SWEPT_EDGE",EDGE,{"disambiguationData":[OSD([subQ7,subQ6,subQ11,subQ10])]});Q24=makeQuery(id+"F5.boolean.opBoolean","SPLIT",EDGE,{"disambiguationData":[TD([makeQuery(id+"F5.opExtrude","SWEPT_FACE",FACE,{"disambiguationData":[OSD([subQ19]),TDD([makeQuery(id+"F4.imprint","IMPRINT",EDGE,{"disambiguationData":[TD([[makeQuery(id+"F4.imprint","INTERSECT",VERTEX,{"derivedFrom":[subQ20,subQ19]}),-1.0]])],"derivedFrom":subQ19})])]})])],"derivedFrom":subQ21});}
            var Q25;
            {var subQ4=sQuery(id+"F2.wireOp",EDGE,"E20.right");var subQ5=sQuery(id+"F2.wireOp",EDGE,"E20.bottom");var subQ6=sQuery(id+"F0.wireOp",EDGE,"E6");var subQ7=sQuery(id+"F0.wireOp",EDGE,"E4");var subQ8=sQuery(id+"F2.wireOp",EDGE,"E20.top");var subQ25=makeQuery(id+"F3.opExtrude","SWEPT_EDGE",EDGE,{"disambiguationData":[OSD([subQ7,subQ6,subQ5,subQ4])]});Q25=makeQuery(id+"F5.boolean.opBoolean","SPLIT",EDGE,{"disambiguationData":[TD([makeQuery(id+"F3.opExtrude","CAP_FACE",FACE,{"disambiguationData":[OSD([subQ5,subQ8,sQuery(id+"F2.wireOp",EDGE,"E20.left"),subQ4])],"isStart":false})])],"derivedFrom":subQ25});}
            var Q26;
            {var subQ0=sQuery(id+"F4.wireOp",EDGE,"E29");var subQ1=sQuery(id+"F0.wireOp",EDGE,"E6");var subQ2=sQuery(id+"F0.wireOp",EDGE,"E4");Q26=makeQuery(id+"F5.opExtrude","CAP_EDGE",EDGE,{"disambiguationData":[OSD([subQ0]),TDD([makeQuery(id+"F4.imprint","IMPRINT",EDGE,{"disambiguationData":[TD([[makeQuery(id+"F4.imprint","INTERSECT",VERTEX,{"derivedFrom":[makeQuery(id+"F3.opExtrude","SWEPT_EDGE",EDGE,{"disambiguationData":[OSD([subQ2,subQ1,sQuery(id+"F2.wireOp",EDGE,"E19.top"),sQuery(id+"F2.wireOp",EDGE,"E19.right")])]}),subQ0]}),-1.0]])],"derivedFrom":subQ0})])],"isStart":true});}
            var Q27;
            {var subQ0=sQuery(id+"F4.wireOp",EDGE,"E31");var subQ1=sQuery(id+"F0.wireOp",EDGE,"E6");var subQ2=sQuery(id+"F0.wireOp",EDGE,"E4");Q27=makeQuery(id+"F5.opExtrude","CAP_EDGE",EDGE,{"disambiguationData":[OSD([subQ0]),TDD([makeQuery(id+"F4.imprint","IMPRINT",EDGE,{"disambiguationData":[TD([[makeQuery(id+"F4.imprint","INTERSECT",VERTEX,{"derivedFrom":[makeQuery(id+"F3.opExtrude","SWEPT_EDGE",EDGE,{"disambiguationData":[OSD([subQ2,subQ1,sQuery(id+"F2.wireOp",EDGE,"E20.top"),sQuery(id+"F2.wireOp",EDGE,"E20.right")])]}),subQ0]}),-1.0]])],"derivedFrom":subQ0})])],"isStart":true});}
            var Q28;
            {var subQ6=sQuery(id+"F0.wireOp",EDGE,"E6");var subQ7=sQuery(id+"F0.wireOp",EDGE,"E4");var subQ10=sQuery(id+"F2.wireOp",EDGE,"E20.right");var subQ16=sQuery(id+"F4.wireOp",EDGE,"E27");var subQ20=sQuery(id+"F2.wireOp",EDGE,"E20.top");var subQ25=makeQuery(id+"F3.opExtrude","SWEPT_EDGE",EDGE,{"disambiguationData":[OSD([subQ7,subQ6,subQ20,subQ10])]});Q28=makeQuery(id+"F5.boolean.opBoolean","SPLIT",EDGE,{"disambiguationData":[TD([makeQuery(id+"F5.opExtrude","SWEPT_FACE",FACE,{"disambiguationData":[OSD([subQ16]),TDD([makeQuery(id+"F4.imprint","IMPRINT",EDGE,{"disambiguationData":[TD([[makeQuery(id+"F4.imprint","INTERSECT",VERTEX,{"derivedFrom":[subQ25,subQ16]}),-1.0]])],"derivedFrom":subQ16})])]})])],"derivedFrom":subQ25});}
            var Q29;
            {var subQ0=sQuery(id+"F4.wireOp",EDGE,"E27");var subQ1=sQuery(id+"F0.wireOp",EDGE,"E6");var subQ2=sQuery(id+"F0.wireOp",EDGE,"E4");Q29=makeQuery(id+"F5.opExtrude","CAP_EDGE",EDGE,{"disambiguationData":[OSD([subQ0]),TDD([makeQuery(id+"F4.imprint","IMPRINT",EDGE,{"disambiguationData":[TD([[makeQuery(id+"F4.imprint","INTERSECT",VERTEX,{"derivedFrom":[makeQuery(id+"F3.opExtrude","SWEPT_EDGE",EDGE,{"disambiguationData":[OSD([subQ2,subQ1,sQuery(id+"F2.wireOp",EDGE,"E20.top"),sQuery(id+"F2.wireOp",EDGE,"E20.right")])]}),subQ0]}),-1.0]])],"derivedFrom":subQ0})])],"isStart":true});}
            var Q30;
            {var subQ0=sQuery(id+"F4.wireOp",EDGE,"E25");var subQ1=sQuery(id+"F0.wireOp",EDGE,"E6");var subQ2=sQuery(id+"F0.wireOp",EDGE,"E4");Q30=makeQuery(id+"F5.opExtrude","CAP_EDGE",EDGE,{"disambiguationData":[OSD([subQ0]),TDD([makeQuery(id+"F4.imprint","IMPRINT",EDGE,{"disambiguationData":[TD([[makeQuery(id+"F4.imprint","INTERSECT",VERTEX,{"derivedFrom":[makeQuery(id+"F3.opExtrude","SWEPT_EDGE",EDGE,{"disambiguationData":[OSD([subQ2,subQ1,sQuery(id+"F2.wireOp",EDGE,"E19.top"),sQuery(id+"F2.wireOp",EDGE,"E19.right")])]}),subQ0]}),-1.0]])],"derivedFrom":subQ0})])],"isStart":true});}
            var Q31;
            {var subQ4=sQuery(id+"F2.wireOp",EDGE,"E20.right");var subQ5=sQuery(id+"F2.wireOp",EDGE,"E20.bottom");var subQ6=sQuery(id+"F0.wireOp",EDGE,"E6");var subQ7=sQuery(id+"F0.wireOp",EDGE,"E4");var subQ20=makeQuery(id+"F3.opExtrude","SWEPT_EDGE",EDGE,{"disambiguationData":[OSD([subQ7,subQ6,subQ5,subQ4])]});Q31=makeQuery(id+"F5.boolean.opBoolean","SPLIT",EDGE,{"disambiguationData":[TD([makeQuery(id+"F1.opExtrude","SWEPT_FACE",FACE,{"disambiguationData":[OSD([subQ7])]})])],"derivedFrom":subQ20});}
            var Q32;
            {var subQ4=sQuery(id+"F2.wireOp",EDGE,"E20.right");var subQ5=sQuery(id+"F2.wireOp",EDGE,"E20.bottom");var subQ6=sQuery(id+"F0.wireOp",EDGE,"E6");var subQ7=sQuery(id+"F0.wireOp",EDGE,"E4");var subQ24=sQuery(id+"F2.wireOp",EDGE,"E20.top");var subQ25=makeQuery(id+"F3.opExtrude","SWEPT_EDGE",EDGE,{"disambiguationData":[OSD([subQ7,subQ6,subQ24,subQ4])]});Q32=makeQuery(id+"F5.boolean.opBoolean","SPLIT",EDGE,{"disambiguationData":[TD([makeQuery(id+"F3.opExtrude","CAP_FACE",FACE,{"disambiguationData":[OSD([subQ5,subQ24,sQuery(id+"F2.wireOp",EDGE,"E20.left"),subQ4])],"isStart":false})])],"derivedFrom":subQ25});}
            var Q33;
            {var subQ4=sQuery(id+"F2.wireOp",EDGE,"E20.right");var subQ6=sQuery(id+"F0.wireOp",EDGE,"E6");var subQ7=sQuery(id+"F0.wireOp",EDGE,"E4");var subQ17=sQuery(id+"F2.wireOp",EDGE,"E20.top");var subQ20=makeQuery(id+"F3.opExtrude","SWEPT_EDGE",EDGE,{"disambiguationData":[OSD([subQ7,subQ6,subQ17,subQ4])]});Q33=makeQuery(id+"F5.boolean.opBoolean","SPLIT",EDGE,{"disambiguationData":[TD([makeQuery(id+"F1.opExtrude","SWEPT_FACE",FACE,{"disambiguationData":[OSD([subQ7])]})])],"derivedFrom":subQ20});}
            var Q34;
            {var subQ6=sQuery(id+"F0.wireOp",EDGE,"E6");var subQ7=sQuery(id+"F0.wireOp",EDGE,"E4");var subQ9=sQuery(id+"F2.wireOp",EDGE,"E19.right");var subQ10=sQuery(id+"F2.wireOp",EDGE,"E19.top");var subQ16=makeQuery(id+"F3.opExtrude","SWEPT_EDGE",EDGE,{"disambiguationData":[OSD([subQ7,subQ6,subQ10,subQ9])]});var subQ21=sQuery(id+"F2.wireOp",EDGE,"E19.bottom");Q34=makeQuery(id+"F5.boolean.opBoolean","SPLIT",EDGE,{"disambiguationData":[TD([makeQuery(id+"F3.opExtrude","CAP_FACE",FACE,{"disambiguationData":[OSD([subQ21,subQ10,sQuery(id+"F2.wireOp",EDGE,"E19.left"),subQ9])],"isStart":false})])],"derivedFrom":subQ16});}
            var Q35;
            {var subQ6=sQuery(id+"F0.wireOp",EDGE,"E6");var subQ7=sQuery(id+"F0.wireOp",EDGE,"E4");var subQ10=sQuery(id+"F2.wireOp",EDGE,"E20.right");var subQ12=sQuery(id+"F2.wireOp",EDGE,"E20.top");var subQ13=sQuery(id+"F2.wireOp",EDGE,"E19.right");var subQ14=sQuery(id+"F2.wireOp",EDGE,"E19.top");var subQ15=sQuery(id+"F4.wireOp",EDGE,"E27");var subQ19=makeQuery(id+"F3.opExtrude","SWEPT_EDGE",EDGE,{"disambiguationData":[OSD([subQ7,subQ6,subQ12,subQ10])]});var subQ20=makeQuery(id+"F3.opExtrude","SWEPT_EDGE",EDGE,{"disambiguationData":[OSD([subQ7,subQ6,subQ14,subQ13])]});Q35=makeQuery(id+"F5.boolean.opBoolean","SPLIT",EDGE,{"disambiguationData":[TD([makeQuery(id+"F5.opExtrude","SWEPT_FACE",FACE,{"disambiguationData":[OSD([subQ15]),TDD([makeQuery(id+"F4.imprint","IMPRINT",EDGE,{"disambiguationData":[TD([[makeQuery(id+"F4.imprint","INTERSECT",VERTEX,{"derivedFrom":[subQ19,subQ15]}),-1.0]])],"derivedFrom":subQ15})])]})])],"derivedFrom":subQ20});}
            var Q36;
            {var subQ6=sQuery(id+"F0.wireOp",EDGE,"E6");var subQ7=sQuery(id+"F0.wireOp",EDGE,"E4");var subQ9=sQuery(id+"F2.wireOp",EDGE,"E19.right");var subQ10=sQuery(id+"F2.wireOp",EDGE,"E19.top");var subQ16=makeQuery(id+"F3.opExtrude","SWEPT_EDGE",EDGE,{"disambiguationData":[OSD([subQ7,subQ6,subQ10,subQ9])]});Q36=makeQuery(id+"F5.boolean.opBoolean","SPLIT",EDGE,{"disambiguationData":[TD([makeQuery(id+"F1.opExtrude","SWEPT_FACE",FACE,{"disambiguationData":[OSD([subQ7])]})])],"derivedFrom":subQ16});}
            var Q37;
            {var subQ0=sQuery(id+"F4.wireOp",EDGE,"E25");var subQ1=sQuery(id+"F0.wireOp",EDGE,"E6");var subQ2=sQuery(id+"F0.wireOp",EDGE,"E4");Q37=makeQuery(id+"F5.opExtrude","CAP_EDGE",EDGE,{"disambiguationData":[OSD([subQ0]),TDD([makeQuery(id+"F4.imprint","IMPRINT",EDGE,{"disambiguationData":[TD([[makeQuery(id+"F4.imprint","INTERSECT",VERTEX,{"derivedFrom":[makeQuery(id+"F3.opExtrude","SWEPT_EDGE",EDGE,{"disambiguationData":[OSD([subQ2,subQ1,sQuery(id+"F2.wireOp",EDGE,"E18.top"),sQuery(id+"F2.wireOp",EDGE,"E18.right")])]}),subQ0]}),-1.0]])],"derivedFrom":subQ0})])],"isStart":true});}
            var Q38;
            {var subQ0=sQuery(id+"F4.wireOp",EDGE,"E27");var subQ1=sQuery(id+"F0.wireOp",EDGE,"E6");var subQ2=sQuery(id+"F0.wireOp",EDGE,"E4");Q38=makeQuery(id+"F5.opExtrude","CAP_EDGE",EDGE,{"disambiguationData":[OSD([subQ0]),TDD([makeQuery(id+"F4.imprint","IMPRINT",EDGE,{"disambiguationData":[TD([[makeQuery(id+"F4.imprint","INTERSECT",VERTEX,{"derivedFrom":[makeQuery(id+"F3.opExtrude","SWEPT_EDGE",EDGE,{"disambiguationData":[OSD([subQ2,subQ1,sQuery(id+"F2.wireOp",EDGE,"E19.bottom"),sQuery(id+"F2.wireOp",EDGE,"E19.right")])]}),subQ0]}),-1.0]])],"derivedFrom":subQ0})])],"isStart":true});}
            var Q39;
            {var subQ6=sQuery(id+"F0.wireOp",EDGE,"E6");var subQ7=sQuery(id+"F0.wireOp",EDGE,"E4");var subQ13=sQuery(id+"F2.wireOp",EDGE,"E19.right");var subQ19=sQuery(id+"F4.wireOp",EDGE,"E27");var subQ23=sQuery(id+"F2.wireOp",EDGE,"E19.bottom");var subQ24=makeQuery(id+"F3.opExtrude","SWEPT_EDGE",EDGE,{"disambiguationData":[OSD([subQ7,subQ6,subQ23,subQ13])]});Q39=makeQuery(id+"F5.boolean.opBoolean","SPLIT",EDGE,{"disambiguationData":[TD([makeQuery(id+"F5.opExtrude","SWEPT_FACE",FACE,{"disambiguationData":[OSD([subQ19]),TDD([makeQuery(id+"F4.imprint","IMPRINT",EDGE,{"disambiguationData":[TD([[makeQuery(id+"F4.imprint","INTERSECT",VERTEX,{"derivedFrom":[subQ24,subQ19]}),-1.0]])],"derivedFrom":subQ19})])]})])],"derivedFrom":subQ24});}
            var Q40;
            {var subQ0=sQuery(id+"F4.wireOp",EDGE,"E31");var subQ1=sQuery(id+"F0.wireOp",EDGE,"E6");var subQ2=sQuery(id+"F0.wireOp",EDGE,"E4");Q40=makeQuery(id+"F5.opExtrude","CAP_EDGE",EDGE,{"disambiguationData":[OSD([subQ0]),TDD([makeQuery(id+"F4.imprint","IMPRINT",EDGE,{"disambiguationData":[TD([[makeQuery(id+"F4.imprint","INTERSECT",VERTEX,{"derivedFrom":[makeQuery(id+"F3.opExtrude","SWEPT_EDGE",EDGE,{"disambiguationData":[OSD([subQ2,subQ1,sQuery(id+"F2.wireOp",EDGE,"E19.bottom"),sQuery(id+"F2.wireOp",EDGE,"E19.right")])]}),subQ0]}),-1.0]])],"derivedFrom":subQ0})])],"isStart":true});}
            var Q41;
            {var subQ0=sQuery(id+"F4.wireOp",EDGE,"E29");var subQ1=sQuery(id+"F0.wireOp",EDGE,"E6");var subQ2=sQuery(id+"F0.wireOp",EDGE,"E4");Q41=makeQuery(id+"F5.opExtrude","CAP_EDGE",EDGE,{"disambiguationData":[OSD([subQ0]),TDD([makeQuery(id+"F4.imprint","IMPRINT",EDGE,{"disambiguationData":[TD([[makeQuery(id+"F4.imprint","INTERSECT",VERTEX,{"derivedFrom":[makeQuery(id+"F3.opExtrude","SWEPT_EDGE",EDGE,{"disambiguationData":[OSD([subQ2,subQ1,sQuery(id+"F2.wireOp",EDGE,"E18.top"),sQuery(id+"F2.wireOp",EDGE,"E18.right")])]}),subQ0]}),-1.0]])],"derivedFrom":subQ0})])],"isStart":true});}
            var Q42;
            {var subQ6=sQuery(id+"F0.wireOp",EDGE,"E6");var subQ7=sQuery(id+"F0.wireOp",EDGE,"E4");var subQ9=sQuery(id+"F2.wireOp",EDGE,"E19.right");var subQ10=sQuery(id+"F2.wireOp",EDGE,"E19.top");var subQ23=sQuery(id+"F2.wireOp",EDGE,"E19.bottom");var subQ25=makeQuery(id+"F3.opExtrude","SWEPT_EDGE",EDGE,{"disambiguationData":[OSD([subQ7,subQ6,subQ23,subQ9])]});Q42=makeQuery(id+"F5.boolean.opBoolean","SPLIT",EDGE,{"disambiguationData":[TD([makeQuery(id+"F3.opExtrude","CAP_FACE",FACE,{"disambiguationData":[OSD([subQ23,subQ10,sQuery(id+"F2.wireOp",EDGE,"E19.left"),subQ9])],"isStart":false})])],"derivedFrom":subQ25});}
            var Q43;
            {var subQ6=sQuery(id+"F0.wireOp",EDGE,"E6");var subQ7=sQuery(id+"F0.wireOp",EDGE,"E4");var subQ11=sQuery(id+"F2.wireOp",EDGE,"E18.right");var subQ12=sQuery(id+"F2.wireOp",EDGE,"E18.bottom");var subQ20=sQuery(id+"F2.wireOp",EDGE,"E18.top");var subQ25=makeQuery(id+"F3.opExtrude","SWEPT_EDGE",EDGE,{"disambiguationData":[OSD([subQ7,subQ6,subQ20,subQ11])]});Q43=makeQuery(id+"F5.boolean.opBoolean","SPLIT",EDGE,{"disambiguationData":[TD([makeQuery(id+"F3.opExtrude","CAP_FACE",FACE,{"disambiguationData":[OSD([subQ12,subQ20,sQuery(id+"F2.wireOp",EDGE,"E18.left"),subQ11])],"isStart":false})])],"derivedFrom":subQ25});}
            var Q44;
            {var subQ0=sQuery(id+"F4.wireOp",EDGE,"E29");var subQ1=sQuery(id+"F0.wireOp",EDGE,"E6");var subQ2=sQuery(id+"F0.wireOp",EDGE,"E4");Q44=makeQuery(id+"F5.opExtrude","CAP_EDGE",EDGE,{"disambiguationData":[OSD([subQ0]),TDD([makeQuery(id+"F4.imprint","IMPRINT",EDGE,{"disambiguationData":[TD([[makeQuery(id+"F4.imprint","INTERSECT",VERTEX,{"derivedFrom":[makeQuery(id+"F3.opExtrude","SWEPT_EDGE",EDGE,{"disambiguationData":[OSD([subQ2,subQ1,sQuery(id+"F2.wireOp",EDGE,"E17.top"),sQuery(id+"F2.wireOp",EDGE,"E17.right")])]}),subQ0]}),-1.0]])],"derivedFrom":subQ0})])],"isStart":true});}
            var Q45;
            {var subQ0=sQuery(id+"F4.wireOp",EDGE,"E31");var subQ1=sQuery(id+"F0.wireOp",EDGE,"E6");var subQ2=sQuery(id+"F0.wireOp",EDGE,"E4");Q45=makeQuery(id+"F5.opExtrude","CAP_EDGE",EDGE,{"disambiguationData":[OSD([subQ0]),TDD([makeQuery(id+"F4.imprint","IMPRINT",EDGE,{"disambiguationData":[TD([[makeQuery(id+"F4.imprint","INTERSECT",VERTEX,{"derivedFrom":[makeQuery(id+"F3.opExtrude","SWEPT_EDGE",EDGE,{"disambiguationData":[OSD([subQ2,subQ1,sQuery(id+"F2.wireOp",EDGE,"E18.bottom"),sQuery(id+"F2.wireOp",EDGE,"E18.right")])]}),subQ0]}),-1.0]])],"derivedFrom":subQ0})])],"isStart":true});}
            var Q46;
            {var subQ6=sQuery(id+"F0.wireOp",EDGE,"E6");var subQ7=sQuery(id+"F0.wireOp",EDGE,"E4");var subQ13=sQuery(id+"F2.wireOp",EDGE,"E19.right");var subQ15=sQuery(id+"F2.wireOp",EDGE,"E18.right");var subQ19=sQuery(id+"F4.wireOp",EDGE,"E27");var subQ23=sQuery(id+"F2.wireOp",EDGE,"E18.top");var subQ24=sQuery(id+"F2.wireOp",EDGE,"E19.bottom");var subQ25=makeQuery(id+"F3.opExtrude","SWEPT_EDGE",EDGE,{"disambiguationData":[OSD([subQ7,subQ6,subQ24,subQ13])]});var subQ26=makeQuery(id+"F3.opExtrude","SWEPT_EDGE",EDGE,{"disambiguationData":[OSD([subQ7,subQ6,subQ23,subQ15])]});Q46=makeQuery(id+"F5.boolean.opBoolean","SPLIT",EDGE,{"disambiguationData":[TD([makeQuery(id+"F5.opExtrude","SWEPT_FACE",FACE,{"disambiguationData":[OSD([subQ19]),TDD([makeQuery(id+"F4.imprint","IMPRINT",EDGE,{"disambiguationData":[TD([[makeQuery(id+"F4.imprint","INTERSECT",VERTEX,{"derivedFrom":[subQ25,subQ19]}),-1.0]])],"derivedFrom":subQ19})])]})])],"derivedFrom":subQ26});}
            var Q47;
            {var subQ6=sQuery(id+"F0.wireOp",EDGE,"E6");var subQ7=sQuery(id+"F0.wireOp",EDGE,"E4");var subQ15=sQuery(id+"F2.wireOp",EDGE,"E18.right");var subQ16=sQuery(id+"F2.wireOp",EDGE,"E18.bottom");var subQ19=sQuery(id+"F4.wireOp",EDGE,"E27");var subQ20=makeQuery(id+"F3.opExtrude","SWEPT_EDGE",EDGE,{"disambiguationData":[OSD([subQ7,subQ6,subQ16,subQ15])]});Q47=makeQuery(id+"F5.boolean.opBoolean","SPLIT",EDGE,{"disambiguationData":[TD([makeQuery(id+"F5.opExtrude","SWEPT_FACE",FACE,{"disambiguationData":[OSD([subQ19]),TDD([makeQuery(id+"F4.imprint","IMPRINT",EDGE,{"disambiguationData":[TD([[makeQuery(id+"F4.imprint","INTERSECT",VERTEX,{"derivedFrom":[subQ20,subQ19]}),-1.0]])],"derivedFrom":subQ19})])]})])],"derivedFrom":subQ20});}
            var Q48;
            {var subQ6=sQuery(id+"F0.wireOp",EDGE,"E6");var subQ7=sQuery(id+"F0.wireOp",EDGE,"E4");var subQ11=sQuery(id+"F2.wireOp",EDGE,"E18.right");var subQ20=sQuery(id+"F2.wireOp",EDGE,"E18.top");var subQ21=makeQuery(id+"F3.opExtrude","SWEPT_EDGE",EDGE,{"disambiguationData":[OSD([subQ7,subQ6,subQ20,subQ11])]});Q48=makeQuery(id+"F5.boolean.opBoolean","SPLIT",EDGE,{"disambiguationData":[TD([makeQuery(id+"F1.opExtrude","SWEPT_FACE",FACE,{"disambiguationData":[OSD([subQ7])]})])],"derivedFrom":subQ21});}
            var Q49;
            {var subQ6=sQuery(id+"F0.wireOp",EDGE,"E6");var subQ7=sQuery(id+"F0.wireOp",EDGE,"E4");var subQ11=sQuery(id+"F2.wireOp",EDGE,"E18.right");var subQ12=sQuery(id+"F2.wireOp",EDGE,"E18.bottom");var subQ20=makeQuery(id+"F3.opExtrude","SWEPT_EDGE",EDGE,{"disambiguationData":[OSD([subQ7,subQ6,subQ12,subQ11])]});var subQ21=sQuery(id+"F2.wireOp",EDGE,"E18.top");Q49=makeQuery(id+"F5.boolean.opBoolean","SPLIT",EDGE,{"disambiguationData":[TD([makeQuery(id+"F3.opExtrude","CAP_FACE",FACE,{"disambiguationData":[OSD([subQ12,subQ21,sQuery(id+"F2.wireOp",EDGE,"E18.left"),subQ11])],"isStart":false})])],"derivedFrom":subQ20});}
            var Q50;
            {var subQ6=sQuery(id+"F0.wireOp",EDGE,"E6");var subQ7=sQuery(id+"F0.wireOp",EDGE,"E4");var subQ13=sQuery(id+"F2.wireOp",EDGE,"E17.right");var subQ14=sQuery(id+"F2.wireOp",EDGE,"E17.top");var subQ17=makeQuery(id+"F3.opExtrude","SWEPT_EDGE",EDGE,{"disambiguationData":[OSD([subQ7,subQ6,subQ14,subQ13])]});Q50=makeQuery(id+"F5.boolean.opBoolean","SPLIT",EDGE,{"disambiguationData":[TD([makeQuery(id+"F3.opExtrude","CAP_FACE",FACE,{"disambiguationData":[OSD([sQuery(id+"F2.wireOp",EDGE,"E17.bottom"),subQ14,sQuery(id+"F2.wireOp",EDGE,"E17.left"),subQ13])],"isStart":false})])],"derivedFrom":subQ17});}
            var Q51;
            Q51=makeQuery(id+"F3.opExtrude","SWEPT_EDGE",EDGE,{"disambiguationData":[OSD([sQuery(id+"F0.wireOp",EDGE,"E4"),sQuery(id+"F0.wireOp",EDGE,"E6"),sQuery(id+"F2.wireOp",EDGE,"E17.bottom"),sQuery(id+"F2.wireOp",EDGE,"E17.right")])]});
            var Q52;
            {var subQ6=sQuery(id+"F0.wireOp",EDGE,"E6");var subQ7=sQuery(id+"F0.wireOp",EDGE,"E4");var subQ15=sQuery(id+"F2.wireOp",EDGE,"E18.right");var subQ16=sQuery(id+"F2.wireOp",EDGE,"E18.bottom");var subQ17=sQuery(id+"F2.wireOp",EDGE,"E17.right");var subQ18=sQuery(id+"F2.wireOp",EDGE,"E17.top");var subQ19=sQuery(id+"F4.wireOp",EDGE,"E27");var subQ20=makeQuery(id+"F3.opExtrude","SWEPT_EDGE",EDGE,{"disambiguationData":[OSD([subQ7,subQ6,subQ16,subQ15])]});var subQ21=makeQuery(id+"F3.opExtrude","SWEPT_EDGE",EDGE,{"disambiguationData":[OSD([subQ7,subQ6,subQ18,subQ17])]});Q52=makeQuery(id+"F5.boolean.opBoolean","SPLIT",EDGE,{"disambiguationData":[TD([makeQuery(id+"F5.opExtrude","SWEPT_FACE",FACE,{"disambiguationData":[OSD([subQ19]),TDD([makeQuery(id+"F4.imprint","IMPRINT",EDGE,{"disambiguationData":[TD([[makeQuery(id+"F4.imprint","INTERSECT",VERTEX,{"derivedFrom":[subQ20,subQ19]}),-1.0]])],"derivedFrom":subQ19})])]})])],"derivedFrom":subQ21});}
            var Q53;
            {var subQ0=sQuery(id+"F4.wireOp",EDGE,"E27");var subQ1=sQuery(id+"F0.wireOp",EDGE,"E6");var subQ2=sQuery(id+"F0.wireOp",EDGE,"E4");Q53=makeQuery(id+"F5.opExtrude","CAP_EDGE",EDGE,{"disambiguationData":[OSD([subQ0]),TDD([makeQuery(id+"F4.imprint","IMPRINT",EDGE,{"disambiguationData":[TD([[makeQuery(id+"F4.imprint","INTERSECT",VERTEX,{"derivedFrom":[makeQuery(id+"F3.opExtrude","SWEPT_EDGE",EDGE,{"disambiguationData":[OSD([subQ2,subQ1,sQuery(id+"F2.wireOp",EDGE,"E18.bottom"),sQuery(id+"F2.wireOp",EDGE,"E18.right")])]}),subQ0]}),-1.0]])],"derivedFrom":subQ0})])],"isStart":true});}
            var Q54;
            {var subQ0=sQuery(id+"F4.wireOp",EDGE,"E25");var subQ1=sQuery(id+"F0.wireOp",EDGE,"E6");var subQ2=sQuery(id+"F0.wireOp",EDGE,"E4");Q54=makeQuery(id+"F5.opExtrude","CAP_EDGE",EDGE,{"disambiguationData":[OSD([subQ0]),TDD([makeQuery(id+"F4.imprint","IMPRINT",EDGE,{"disambiguationData":[TD([[makeQuery(id+"F4.imprint","INTERSECT",VERTEX,{"derivedFrom":[makeQuery(id+"F3.opExtrude","SWEPT_EDGE",EDGE,{"disambiguationData":[OSD([subQ2,subQ1,sQuery(id+"F2.wireOp",EDGE,"E17.top"),sQuery(id+"F2.wireOp",EDGE,"E17.right")])]}),subQ0]}),-1.0]])],"derivedFrom":subQ0})])],"isStart":true});}
            var Q55;
            {var subQ6=sQuery(id+"F0.wireOp",EDGE,"E6");var subQ7=sQuery(id+"F0.wireOp",EDGE,"E4");var subQ13=sQuery(id+"F2.wireOp",EDGE,"E17.right");var subQ14=sQuery(id+"F2.wireOp",EDGE,"E17.top");var subQ17=makeQuery(id+"F3.opExtrude","SWEPT_EDGE",EDGE,{"disambiguationData":[OSD([subQ7,subQ6,subQ14,subQ13])]});Q55=makeQuery(id+"F5.boolean.opBoolean","SPLIT",EDGE,{"disambiguationData":[TD([makeQuery(id+"F1.opExtrude","SWEPT_FACE",FACE,{"disambiguationData":[OSD([subQ7])]})])],"derivedFrom":subQ17});}
            var Q56;
            {var subQ6=sQuery(id+"F0.wireOp",EDGE,"E6");var subQ7=sQuery(id+"F0.wireOp",EDGE,"E4");var subQ11=sQuery(id+"F2.wireOp",EDGE,"E18.right");var subQ12=sQuery(id+"F2.wireOp",EDGE,"E18.bottom");var subQ20=makeQuery(id+"F3.opExtrude","SWEPT_EDGE",EDGE,{"disambiguationData":[OSD([subQ7,subQ6,subQ12,subQ11])]});Q56=makeQuery(id+"F5.boolean.opBoolean","SPLIT",EDGE,{"disambiguationData":[TD([makeQuery(id+"F1.opExtrude","SWEPT_FACE",FACE,{"disambiguationData":[OSD([subQ7])]})])],"derivedFrom":subQ20});}
            var Q57;
            {var subQ6=sQuery(id+"F0.wireOp",EDGE,"E6");var subQ7=sQuery(id+"F0.wireOp",EDGE,"E4");var subQ9=sQuery(id+"F2.wireOp",EDGE,"E19.right");var subQ21=sQuery(id+"F2.wireOp",EDGE,"E19.bottom");var subQ22=makeQuery(id+"F3.opExtrude","SWEPT_EDGE",EDGE,{"disambiguationData":[OSD([subQ7,subQ6,subQ21,subQ9])]});Q57=makeQuery(id+"F5.boolean.opBoolean","SPLIT",EDGE,{"disambiguationData":[TD([makeQuery(id+"F1.opExtrude","SWEPT_FACE",FACE,{"disambiguationData":[OSD([subQ7])]})])],"derivedFrom":subQ22});}
            var Q58;
            {var subQ0=sQuery(id+"F4.wireOp",EDGE,"E31");var subQ1=sQuery(id+"F0.wireOp",EDGE,"E6");var subQ2=sQuery(id+"F0.wireOp",EDGE,"E4");Q58=makeQuery(id+"F5.opExtrude","CAP_EDGE",EDGE,{"disambiguationData":[OSD([subQ0]),TDD([makeQuery(id+"F4.imprint","IMPRINT",EDGE,{"disambiguationData":[TD([[makeQuery(id+"F4.imprint","INTERSECT",VERTEX,{"derivedFrom":[makeQuery(id+"F3.opExtrude","SWEPT_EDGE",EDGE,{"disambiguationData":[OSD([subQ2,subQ1,sQuery(id+"F2.wireOp",EDGE,"E21.top"),sQuery(id+"F2.wireOp",EDGE,"E21.right")])]}),subQ0]}),-1.0]])],"derivedFrom":subQ0})])],"isStart":true});}
            var Q59;
            {var subQ6=sQuery(id+"F0.wireOp",EDGE,"E6");var subQ7=sQuery(id+"F0.wireOp",EDGE,"E4");var subQ16=sQuery(id+"F2.wireOp",EDGE,"E21.right");var subQ17=sQuery(id+"F2.wireOp",EDGE,"E21.bottom");var subQ18=makeQuery(id+"F3.opExtrude","SWEPT_EDGE",EDGE,{"disambiguationData":[OSD([subQ7,subQ6,subQ17,subQ16])]});Q59=makeQuery(id+"F5.boolean.opBoolean","SPLIT",EDGE,{"disambiguationData":[TD([makeQuery(id+"F1.opExtrude","SWEPT_FACE",FACE,{"disambiguationData":[OSD([subQ7])]})])],"derivedFrom":subQ18});}
            var Q60;
            {var subQ4=sQuery(id+"F2.wireOp",EDGE,"E22.right");var subQ6=sQuery(id+"F0.wireOp",EDGE,"E6");var subQ7=sQuery(id+"F0.wireOp",EDGE,"E4");var subQ16=sQuery(id+"F4.wireOp",EDGE,"E27");var subQ17=sQuery(id+"F2.wireOp",EDGE,"E22.top");var subQ18=makeQuery(id+"F3.opExtrude","SWEPT_EDGE",EDGE,{"disambiguationData":[OSD([subQ7,subQ6,subQ17,subQ4])]});var subQ19=sQuery(id+"F2.wireOp",EDGE,"E21.right");var subQ20=sQuery(id+"F2.wireOp",EDGE,"E21.bottom");var subQ21=makeQuery(id+"F3.opExtrude","SWEPT_EDGE",EDGE,{"disambiguationData":[OSD([subQ7,subQ6,subQ20,subQ19])]});Q60=makeQuery(id+"F5.boolean.opBoolean","SPLIT",EDGE,{"disambiguationData":[TD([makeQuery(id+"F5.opExtrude","SWEPT_FACE",FACE,{"disambiguationData":[OSD([subQ16]),TDD([makeQuery(id+"F4.imprint","IMPRINT",EDGE,{"disambiguationData":[TD([[makeQuery(id+"F4.imprint","INTERSECT",VERTEX,{"derivedFrom":[subQ18,subQ16]}),-1.0]])],"derivedFrom":subQ16})])]})])],"derivedFrom":subQ21});}
            var Q61;
            {var subQ2=sQuery(id+"F2.wireOp",EDGE,"E21.right");var subQ3=sQuery(id+"F2.wireOp",EDGE,"E21.top");var subQ6=sQuery(id+"F0.wireOp",EDGE,"E6");var subQ7=sQuery(id+"F0.wireOp",EDGE,"E4");var subQ21=sQuery(id+"F2.wireOp",EDGE,"E21.bottom");var subQ25=makeQuery(id+"F3.opExtrude","SWEPT_EDGE",EDGE,{"disambiguationData":[OSD([subQ7,subQ6,subQ3,subQ2])]});Q61=makeQuery(id+"F5.boolean.opBoolean","SPLIT",EDGE,{"disambiguationData":[TD([makeQuery(id+"F3.opExtrude","CAP_FACE",FACE,{"disambiguationData":[OSD([subQ21,subQ3,sQuery(id+"F2.wireOp",EDGE,"E21.left"),subQ2])],"isStart":false})])],"derivedFrom":subQ25});}
            fillet(context, id + "F6", {"entities" : qUnion([Q0, Q1, Q2, Q3, Q4, Q5, Q6, Q7, Q8, Q9, Q10, Q11, Q12, Q13, Q14, Q15, Q16, Q17, Q18, Q19, Q20, Q21, Q22, Q23, Q24, Q25, Q26, Q27, Q28, Q29, Q30, Q31, Q32, Q33, Q34, Q35, Q36, Q37, Q38, Q39, Q40, Q41, Q42, Q43, Q44, Q45, Q46, Q47, Q48, Q49, Q50, Q51, Q52, Q53, Q54, Q55, Q56, Q57, Q58, Q59, Q60, Q61]), "radius" : .3 * mm, "tangentPropagation" : true, "allowEdgeOverflow" : false});
        }
    });
